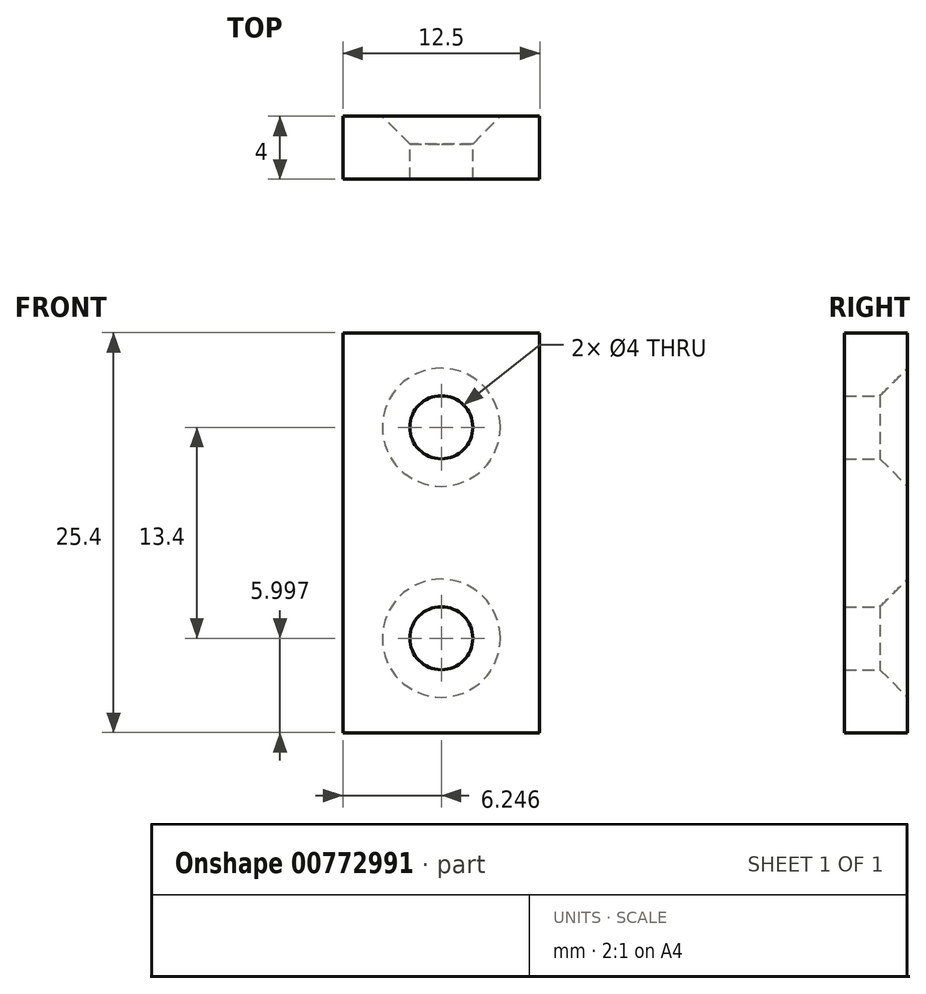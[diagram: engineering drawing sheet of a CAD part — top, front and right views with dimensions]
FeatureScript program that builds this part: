
annotation { "Feature Type Name" : "Feature", "Feature Type Description" : "" }
export const myFeature = defineFeature(function(context is Context, id is Id, definition is map)
    precondition{}
    {
        {
            var Q0;
            Q0=qCreatedBy(makeId("Front.planeOp"),FACE);
            var sketch = newSketch(context, id + "F0", { "sketchPlane" : qUnion([Q0])});
            skLineSegment(sketch, "E0.bottom", {"start": v(-5.55, -3.51) * mm, "end": v(6.95, -3.51) * mm});
            skLineSegment(sketch, "E0.top", {"start": v(-5.55, 21.89) * mm, "end": v(6.95, 21.89) * mm});
            skLineSegment(sketch, "E0.left", {"start": v(-5.55, -3.51) * mm, "end": v(-5.55, 21.89) * mm});
            skLineSegment(sketch, "E0.right", {"start": v(6.95, -3.51) * mm, "end": v(6.95, 21.89) * mm});
            skSolve(sketch);
        }
        {
            var Q0;
            Q0 = qSketchRegion(id + "F0", true);
            extrude(context, id + "F1", {"entities" : qUnion([Q0]), "oppositeDirection" : true, "depth" : 4 * mm, "offsetDistance" : 25 * mm});
        }
        {
            var Q0;
            Q0=makeQuery(id+"F1.opExtrude","CAP_FACE",FACE,{"disambiguationData":[OSD([sQuery(id+"F0.wireOp",EDGE,"E0.bottom"),sQuery(id+"F0.wireOp",EDGE,"E0.top"),sQuery(id+"F0.wireOp",EDGE,"E0.left"),sQuery(id+"F0.wireOp",EDGE,"E0.right")])],"isStart":false});
            var sketch = newSketch(context, id + "F2", { "sketchPlane" : qUnion([Q0])});
            skPoint(sketch, "E1", {"position": v(-0.7, 2.49) * mm});
            skPoint(sketch, "E2", {"position": v(-0.7, 15.89) * mm});
            skSolve(sketch);
        }
        {
            var Q0;
            Q0=sQuery(id+"F2.wireOp",VERTEX,"E2");
            var Q1;
            Q1=sQuery(id+"F2.wireOp",VERTEX,"E1");
            var Q2;
            Q2=makeQuery(id+"F1.opExtrude","SWEPT_BODY",BODY,{"disambiguationData":[OSD([sQuery(id+"F0.wireOp",EDGE,"E0.bottom"),sQuery(id+"F0.wireOp",EDGE,"E0.top"),sQuery(id+"F0.wireOp",EDGE,"E0.left"),sQuery(id+"F0.wireOp",EDGE,"E0.right")])]});
            hole(context, id + "F3", {"style" : HoleStyle.C_SINK, "endStyle" : HoleEndStyle.THROUGH, "holeDiameter" : 4 * mm, "cSinkDiameter" : 7.5 * mm, "cSinkAngle" : 90 * degree, "majorDiameter" : 5 * mm, "isTappedThrough" : true, "tappedDepth" : 12 * mm, "tapClearance" : 3, "locations" : qUnion([Q0, Q1]), "scope" : qUnion([Q2])});
        }
    });
